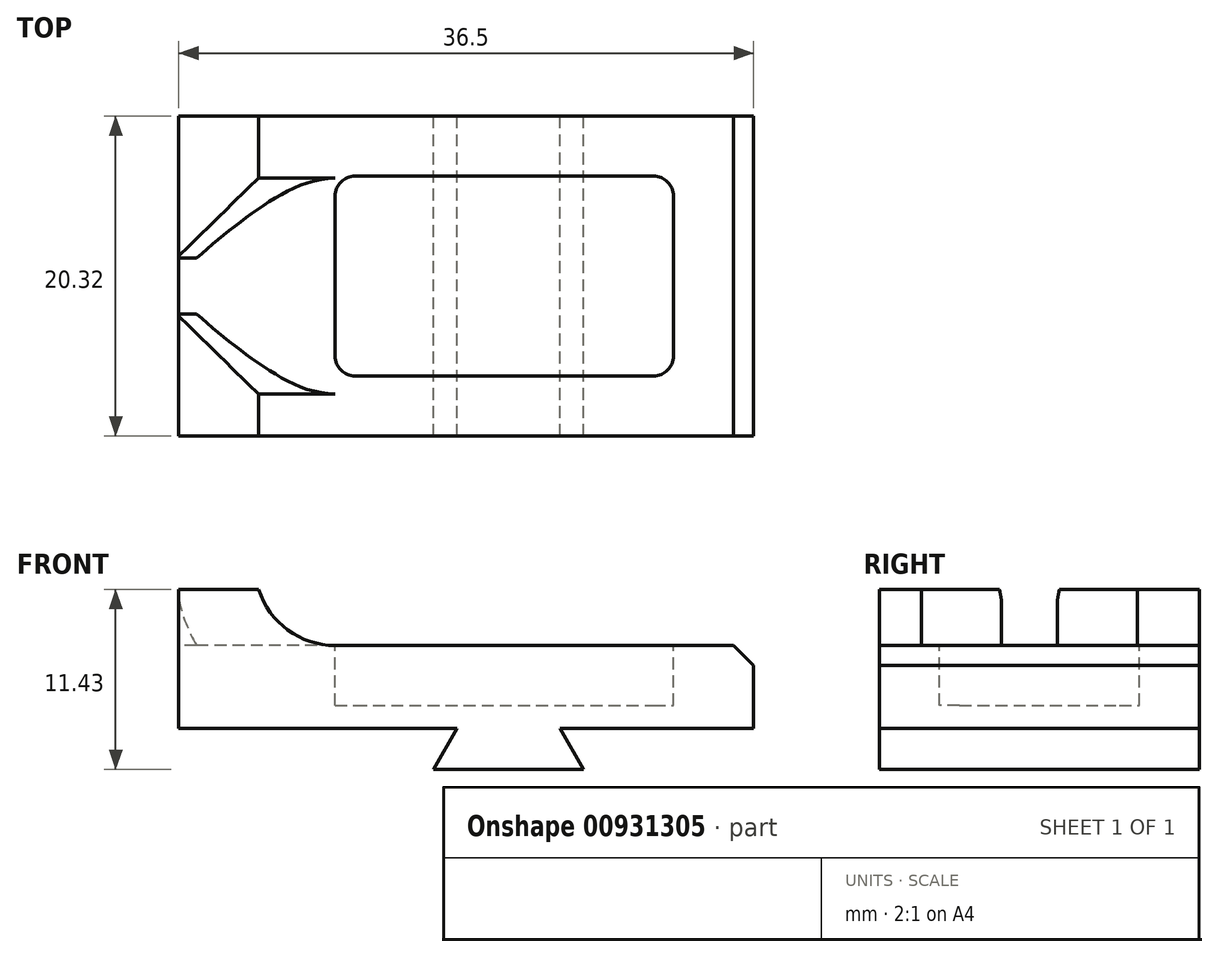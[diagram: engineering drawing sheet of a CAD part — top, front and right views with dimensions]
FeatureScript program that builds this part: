
annotation { "Feature Type Name" : "Feature", "Feature Type Description" : "" }
export const myFeature = defineFeature(function(context is Context, id is Id, definition is map)
    precondition{}
    {
        {
            var Q0;
            Q0=qCreatedBy(makeId("Front.planeOp"),FACE);
            var sketch = newSketch(context, id + "F0", { "sketchPlane" : qUnion([Q0])});
            skLineSegment(sketch, "E0", {"start": v(-21.26, 2.6) * mm, "end": v(-21.26, 11.43) * mm});
            skLineSegment(sketch, "E1", {"start": v(-21.26, 11.43) * mm, "end": v(-16.18, 11.43) * mm});
            skLineSegment(sketch, "E2", {"start": v(-16.18, 11.43) * mm, "end": v(-16.18, 7.87) * mm});
            skLineSegment(sketch, "E3", {"start": v(-16.18, 7.87) * mm, "end": v(15.24, 7.87) * mm});
            skLineSegment(sketch, "E4", {"start": v(15.24, 7.87) * mm, "end": v(15.24, 2.6) * mm});
            skLineSegment(sketch, "E5", {"start": v(15.24, 2.6) * mm, "end": v(2.95, 2.6) * mm});
            skLineSegment(sketch, "E6", {"start": v(2.95, 2.6) * mm, "end": v(4.44, 0) * mm});
            skLineSegment(sketch, "E7", {"start": v(4.44, 0) * mm, "end": v(-5.08, 0) * mm});
            skLineSegment(sketch, "E8", {"start": v(-5.08, 0) * mm, "end": v(-3.58, 2.6) * mm});
            skLineSegment(sketch, "E9", {"start": v(-3.58, 2.6) * mm, "end": v(-21.26, 2.6) * mm});
            skSolve(sketch);
        }
        {
            var Q0;
            Q0=makeQuery(id+"F0.imprint","IMPRINT",FACE,{"disambiguationData":[TD([[makeQuery(id+"F0.imprint","IMPRINT",EDGE,{"derivedFrom":sQuery(id+"F0.wireOp",EDGE,"E0")}),-1.0]])]});
            extrude(context, id + "F1", {"entities" : qUnion([Q0]), "endBound" : BoundingType.SYMMETRIC, "depth" : 20.32 * mm, "offsetDistance" : 25.4 * mm});
        }
        {
            var Q0;
            Q0=makeQuery(id+"F1.opExtrude","SWEPT_FACE",FACE,{"disambiguationData":[OSD([sQuery(id+"F0.wireOp",EDGE,"E0")])]});
            var sketch = newSketch(context, id + "F2", { "sketchPlane" : qUnion([Q0])});
            skLineSegment(sketch, "E10.bottom", {"start": v(-1.14, 11.43) * mm, "end": v(2.41, 11.43) * mm});
            skLineSegment(sketch, "E10.top", {"start": v(-1.14, 7.87) * mm, "end": v(2.41, 7.87) * mm});
            skLineSegment(sketch, "E10.left", {"start": v(-1.14, 11.43) * mm, "end": v(-1.14, 7.87) * mm});
            skLineSegment(sketch, "E10.right", {"start": v(2.41, 11.43) * mm, "end": v(2.41, 7.87) * mm});
            skSolve(sketch);
        }
        {
            var Q0;
            Q0=makeQuery(id+"F2.imprint","IMPRINT",FACE,{"disambiguationData":[TD([[makeQuery(id+"F2.imprint","IMPRINT",EDGE,{"derivedFrom":sQuery(id+"F2.wireOp",EDGE,"E10.bottom")}),1.0]])]});
            extrude(context, id + "F3", {"entities" : qUnion([Q0]), "operationType" : NewBodyOperationType.REMOVE, "oppositeDirection" : true, "depth" : 25.4 * mm, "offsetDistance" : 25.4 * mm});
        }
        {
            var Q0;
            Q0=makeQuery(id+"F1.opExtrude","SWEPT_EDGE",EDGE,{"disambiguationData":[OSD([sQuery(id+"F0.wireOp",EDGE,"E2"),sQuery(id+"F0.wireOp",EDGE,"E3")])]});
            fillet(context, id + "F4", {"entities" : qUnion([Q0]), "radius" : 5.08 * mm, "tangentPropagation" : true, "allowEdgeOverflow" : false});
        }
        {
            var Q0;
            Q0=makeQuery(id+"F1.opExtrude","SWEPT_EDGE",EDGE,{"disambiguationData":[OSD([sQuery(id+"F0.wireOp",EDGE,"E3"),sQuery(id+"F0.wireOp",EDGE,"E4")])]});
            chamfer(context, id + "F5", {"entities" : qUnion([Q0]), "width" : 1.27 * mm, "tangentPropagation" : true});
        }
        {
            var Q0;
            {var subQ0=makeQuery(id+"F3.opExtrude","SWEPT_FACE",FACE,{"disambiguationData":[OSD([sQuery(id+"F2.wireOp",EDGE,"E10.right")])]});var subQ1=sQuery(id+"F0.wireOp",EDGE,"E2");var subQ2=sQuery(id+"F0.wireOp",EDGE,"E3");Q0=makeQuery(id+"F4.opFillet","BLEND_EDGE",EDGE,{"blendedFrom":[makeQuery(id+"F3.boolean.opBoolean","SPLIT",EDGE,{"disambiguationData":[TD([subQ0])],"derivedFrom":makeQuery(id+"F1.opExtrude","SWEPT_EDGE",EDGE,{"disambiguationData":[OSD([subQ1,subQ2])]})}),makeQuery(id+"F3.boolean.opBoolean","COPY",FACE,{"derivedFrom":subQ0})],"blendedInto":[makeQuery(id+"F3.boolean.opBoolean","COPY",FACE,{"derivedFrom":subQ0})]});}
            var Q1;
            {var subQ0=makeQuery(id+"F3.opExtrude","SWEPT_FACE",FACE,{"disambiguationData":[OSD([sQuery(id+"F2.wireOp",EDGE,"E10.left")])]});var subQ1=sQuery(id+"F0.wireOp",EDGE,"E3");var subQ2=sQuery(id+"F0.wireOp",EDGE,"E2");Q1=makeQuery(id+"F4.opFillet","BLEND_EDGE",EDGE,{"blendedFrom":[makeQuery(id+"F3.boolean.opBoolean","SPLIT",EDGE,{"disambiguationData":[TD([subQ0])],"derivedFrom":makeQuery(id+"F1.opExtrude","SWEPT_EDGE",EDGE,{"disambiguationData":[OSD([subQ2,subQ1])]})}),makeQuery(id+"F3.boolean.opBoolean","COPY",FACE,{"derivedFrom":subQ0})],"blendedInto":[makeQuery(id+"F3.boolean.opBoolean","COPY",FACE,{"derivedFrom":subQ0})]});}
            chamfer(context, id + "F6", {"entities" : qUnion([Q0, Q1]), "width" : 5.08 * mm, "tangentPropagation" : true});
        }
        {
            var Q0;
            Q0=makeQuery(id+"F3.boolean.opBoolean","MERGE",FACE,{"derivedFrom":[makeQuery(id+"F1.opExtrude","SWEPT_FACE",FACE,{"disambiguationData":[OSD([sQuery(id+"F0.wireOp",EDGE,"E3")])]})],"fromTools":[makeQuery(id+"F3.opExtrude","SWEPT_FACE",FACE,{"disambiguationData":[OSD([sQuery(id+"F2.wireOp",EDGE,"E10.top")])]})]});
            var sketch = newSketch(context, id + "F7", { "sketchPlane" : qUnion([Q0])});
            skLineSegment(sketch, "E11.bottom", {"start": v(-11.33, 6.35) * mm, "end": v(10.16, 6.35) * mm});
            skLineSegment(sketch, "E11.top", {"start": v(-11.33, -6.35) * mm, "end": v(10.16, -6.35) * mm});
            skLineSegment(sketch, "E11.left", {"start": v(-11.33, 6.35) * mm, "end": v(-11.33, -6.35) * mm});
            skLineSegment(sketch, "E11.right", {"start": v(10.16, 6.35) * mm, "end": v(10.16, -6.35) * mm});
            skSolve(sketch);
        }
        {
            var Q0;
            Q0=makeQuery(id+"F7.imprint","IMPRINT",FACE,{"disambiguationData":[TD([[makeQuery(id+"F7.imprint","IMPRINT",EDGE,{"derivedFrom":sQuery(id+"F7.wireOp",EDGE,"E11.bottom")}),-1.0]])]});
            extrude(context, id + "F8", {"entities" : qUnion([Q0]), "operationType" : NewBodyOperationType.REMOVE, "oppositeDirection" : true, "depth" : 3.8 * mm, "offsetDistance" : 25.4 * mm});
        }
        {
            var Q0;
            Q0=makeQuery(id+"F8.boolean.opBoolean","COPY",EDGE,{"derivedFrom":makeQuery(id+"F8.opExtrude","SWEPT_EDGE",EDGE,{"disambiguationData":[OSD([sQuery(id+"F7.wireOp",EDGE,"E11.bottom"),sQuery(id+"F7.wireOp",EDGE,"E11.left")])]})});
            var Q1;
            Q1=makeQuery(id+"F8.boolean.opBoolean","COPY",EDGE,{"derivedFrom":makeQuery(id+"F8.opExtrude","SWEPT_EDGE",EDGE,{"disambiguationData":[OSD([sQuery(id+"F7.wireOp",EDGE,"E11.bottom"),sQuery(id+"F7.wireOp",EDGE,"E11.right")])]})});
            var Q2;
            Q2=makeQuery(id+"F8.boolean.opBoolean","COPY",EDGE,{"derivedFrom":makeQuery(id+"F8.opExtrude","SWEPT_EDGE",EDGE,{"disambiguationData":[OSD([sQuery(id+"F7.wireOp",EDGE,"E11.top"),sQuery(id+"F7.wireOp",EDGE,"E11.right")])]})});
            var Q3;
            Q3=makeQuery(id+"F8.boolean.opBoolean","COPY",EDGE,{"derivedFrom":makeQuery(id+"F8.opExtrude","SWEPT_EDGE",EDGE,{"disambiguationData":[OSD([sQuery(id+"F7.wireOp",EDGE,"E11.top"),sQuery(id+"F7.wireOp",EDGE,"E11.left")])]})});
            fillet(context, id + "F9", {"entities" : qUnion([Q0, Q1, Q2, Q3]), "radius" : 1.27 * mm, "tangentPropagation" : true, "allowEdgeOverflow" : false});
        }
    });
